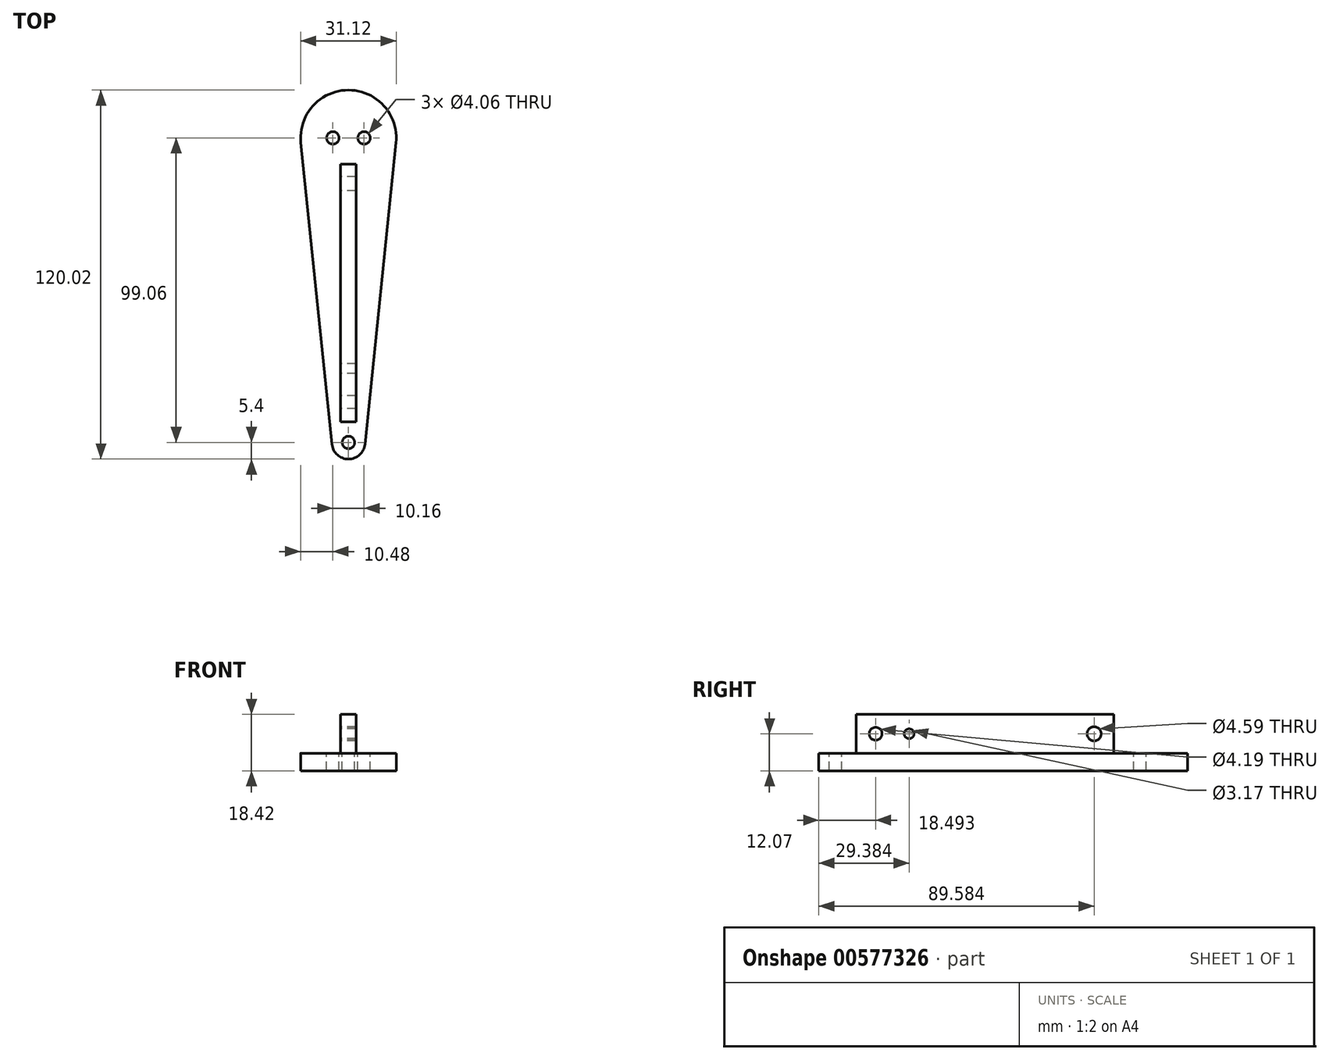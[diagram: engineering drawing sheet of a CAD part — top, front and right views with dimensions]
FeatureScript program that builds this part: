
annotation { "Feature Type Name" : "Feature", "Feature Type Description" : "" }
export const myFeature = defineFeature(function(context is Context, id is Id, definition is map)
    precondition{}
    {
        {
            var Q0;
            Q0=qCreatedBy(makeId("Top.planeOp"),FACE);
            var sketch = newSketch(context, id + "F0", { "sketchPlane" : qUnion([Q0])});
            skArc(sketch, "E0", {"start": v(-5.37, -55.16) * mm, "mid": v(0, -60) * mm, "end": v(5.37, -55.16) * mm});
            skArc(sketch, "E1", {"start": v(15.48, 42.85) * mm, "mid": v(0, 60) * mm, "end": v(-15.48, 42.85) * mm});
            skLineSegment(sketch, "E2", {"start": v(5.37, -55.16) * mm, "end": v(15.48, 42.85) * mm});
            skLineSegment(sketch, "E3", {"start": v(-15.48, 42.85) * mm, "end": v(-5.37, -55.16) * mm});
            skCircle(sketch, "E4", {"center": v(5.08, 44.45) * mm, "radius": 2.03 * mm});
            skCircle(sketch, "E5", {"center": v(0, -54.61) * mm, "radius": 2.03 * mm});
            skCircle(sketch, "E6", {"center": v(-5.08, 44.45) * mm, "radius": 2.03 * mm});
            skSolve(sketch);
        }
        {
            var Q0;
            Q0=makeQuery(id+"F0.imprint","IMPRINT",FACE,{"disambiguationData":[TD([[makeQuery(id+"F0.imprint","IMPRINT",EDGE,{"derivedFrom":sQuery(id+"F0.wireOp",EDGE,"E0")}),1.0]])]});
            extrude(context, id + "F1", {"entities" : qUnion([Q0]), "oppositeDirection" : true, "depth" : 5.7 * mm, "offsetDistance" : 25.4 * mm});
        }
        {
            var Q0;
            Q0=qCreatedBy(makeId("Right.planeOp"),FACE);
            var sketch = newSketch(context, id + "F2", { "sketchPlane" : qUnion([Q0])});
            skLineSegment(sketch, "E7.bottom", {"start": v(35.92, 0) * mm, "end": v(-47.9, 0) * mm});
            skLineSegment(sketch, "E7.top", {"start": v(35.92, 12.7) * mm, "end": v(-47.9, 12.7) * mm});
            skLineSegment(sketch, "E7.left", {"start": v(35.92, 0) * mm, "end": v(35.92, 12.7) * mm});
            skLineSegment(sketch, "E7.right", {"start": v(-47.9, 0) * mm, "end": v(-47.9, 12.7) * mm});
            skCircle(sketch, "E8", {"center": v(29.57, 6.35) * mm, "radius": 2.3 * mm});
            skPoint(sketch, "E8.centerSnap0", {"position": v(35.92, 6.35) * mm});
            skCircle(sketch, "E9", {"center": v(-41.52, 6.35) * mm, "radius": 2.1 * mm});
            skPoint(sketch, "E9.centerSnap0", {"position": v(-47.9, 6.35) * mm});
            skCircle(sketch, "E10", {"center": v(-30.63, 6.35) * mm, "radius": 1.59 * mm});
            skSolve(sketch);
        }
        {
            var Q0;
            Q0=makeQuery(id+"F2.imprint","IMPRINT",FACE,{"disambiguationData":[TD([[makeQuery(id+"F2.imprint","IMPRINT",EDGE,{"derivedFrom":sQuery(id+"F2.wireOp",EDGE,"E7.bottom")}),-1.0]])]});
            extrude(context, id + "F3", {"entities" : qUnion([Q0]), "operationType" : NewBodyOperationType.ADD, "endBound" : BoundingType.SYMMETRIC, "depth" : 5.08 * mm, "offsetDistance" : 25.4 * mm});
        }
    });
